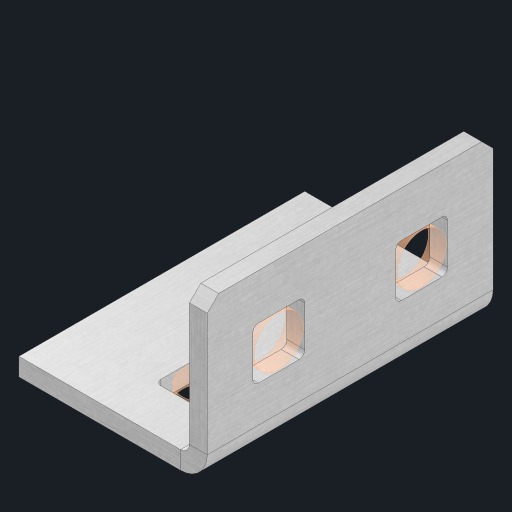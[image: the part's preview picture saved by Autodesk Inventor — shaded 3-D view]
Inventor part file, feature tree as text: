
AUTODESK INVENTOR PART (.ipt)
format: ipt  version: 2023 (Build 270158000, 158)  size: 465,408 bytes
history: native  units: in
note: dims shown in document units (in); Inventor stores cm internally (conversion verified against a paired STEP export)
features: sheet_metal_op x10, other x9, sketch x8, extrude x3, mirror x1, pattern_linear x1, chamfer x1
ambient origin geometry x8: Origin, YZ Plane, XZ Plane, XY Plane, X Axis, Y Axis, Z Axis, Center Point
bodies: Solid1 (feature_tree), Body (feature_tree)
feature tree (33):
  other  "Flange Pattern Plane"
  sheet_metal_op  "Flange Pattern"
  sheet_metal_op  "Body Pattern"
  other  "Arc Length"
  mirror  "Notch Mirror"
  pattern_linear  "Notch Pattern"  Spacing1=0.25in  [1 undecoded]
  chamfer  "End Chamfer"
  extrude  "Half Cut"  Depth=0.0625in
  sketch  "Sketch1"  dims[d0=1.5in]
  other  "Plate1"
  sketch  "Sketch2"  dims[d1=1.0in]
  other  "Plate2"
  sheet_metal_op  "Bend1"
  sheet_metal_op  "Corner1"
  sketch  "Sketch3"  dims[d2=0.0625in]
  other  "Flange Pattern Sketch"
  sketch  "Sketch7"  dims[d3=0.0625in]
  other  "Srf1"
  other  "Srf2"
  sketch  "Sketch8"  dims[d4=0.0312in]
  sketch  "Sketch9"  dims[d5=0.125in]
  other  "Srf91"
  sheet_metal_op  "Body Pattern Sketch"
  other  "Srf92"
  sketch  "Sketch13"  dims[d6=0.0625in]
  sketch  "Sketch14"  dims[d7=0.5in d8=90.0deg d9=0.0312in d10=0.25in d11=0.0625in d12=0.0625in d16=0.182in d17=0.02in d18=0.0625in d19=0.0in d20=0.25in d21=0.25in d46=0.172in d47=1.0in d48=0.0in d49=0.182in d50=0.02in d51=0.25in d52=0.25in d53=0.0625in d54=0.0in d55=0.172in d56=1.0in d57=0.0in d60=0.7874in d62=0.5in d63=0.3937in d65=0.5in d85=0.1473in d86=0.1782in d88=0.04in d89=0.0625in d90=0.0in d91=0.04in d92=0.0491in d95=2.5in d96=0.04in d97=0.25in d98=45.0deg d101=0.0in d102=2.497in d131=0.5in d132=0.7874in d134=0.5in d139=0.5in]
  sheet_metal_op  "Flange Stamp"
  sheet_metal_op  "Flange Circle"
  sheet_metal_op  "Body Stamp"
  sheet_metal_op  "Body Circle"
  sheet_metal_op  "Notch"
  extrude  "ExtrusionSrf2"  Depth=0.0625in
  extrude  "ExtrusionSrf92"  Depth=0.182in
note: 1 required parameter value undecoded (feature->parameter linkage not recoverable at this tier; creation-order binding heuristic only, values carry confidence <= 0.55)
